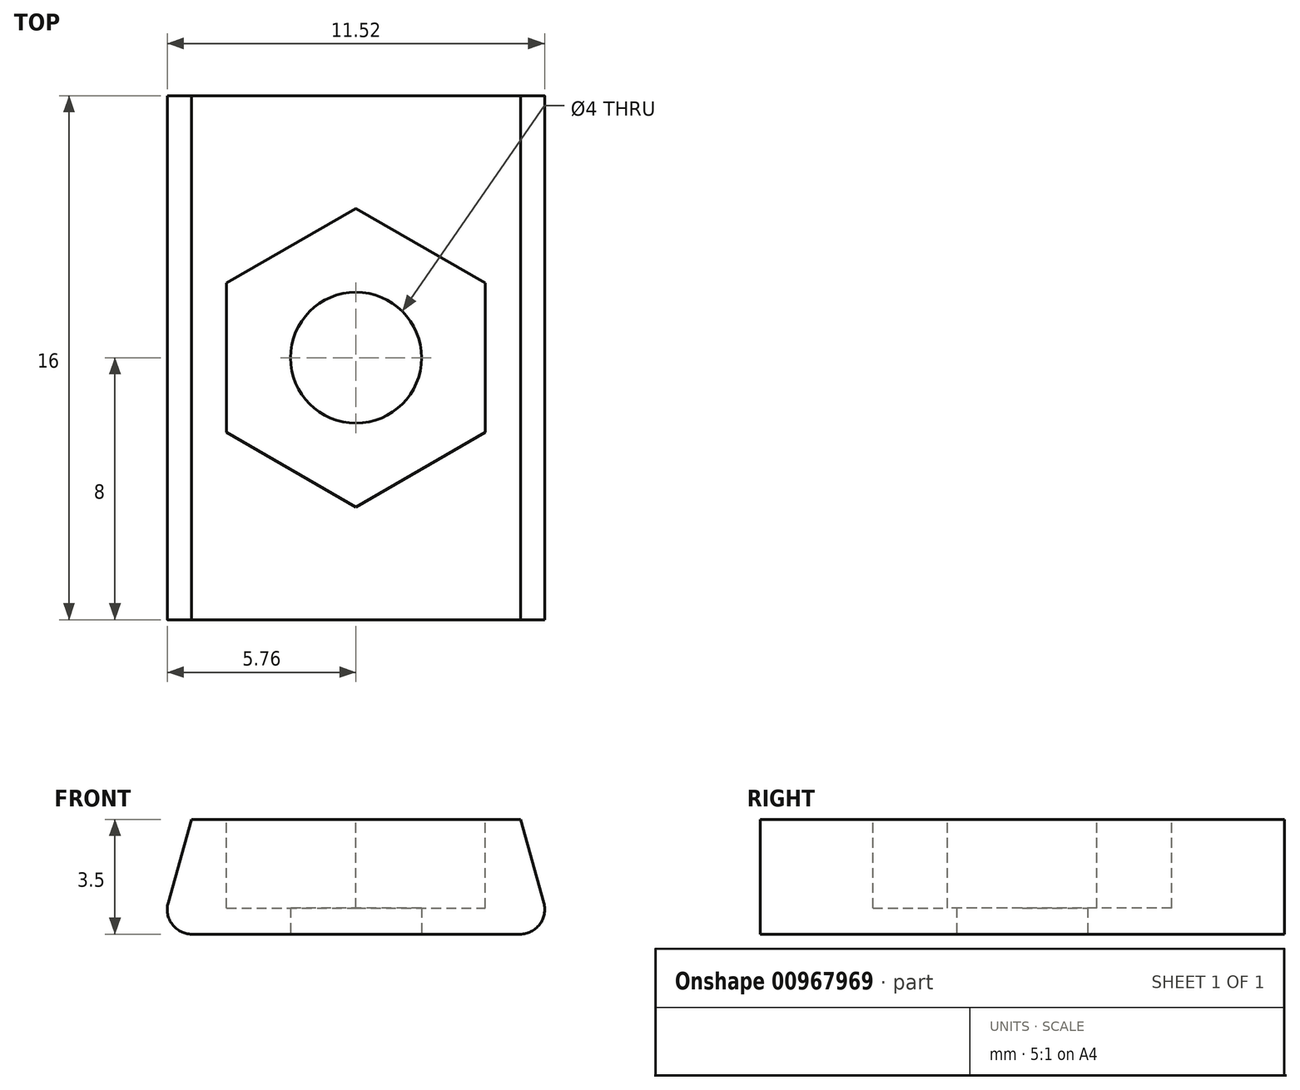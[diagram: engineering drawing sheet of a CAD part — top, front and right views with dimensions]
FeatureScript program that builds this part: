
annotation { "Feature Type Name" : "Feature", "Feature Type Description" : "" }
export const myFeature = defineFeature(function(context is Context, id is Id, definition is map)
    precondition{}
    {
        {
            var Q0;
            Q0=qCreatedBy(makeId("Front.planeOp"),FACE);
            var sketch = newSketch(context, id + "F0", { "sketchPlane" : qUnion([Q0])});
            skLineSegment(sketch, "E0.bottom", {"start": v(6, -2.5) * mm, "end": v(-6, -2.5) * mm});
            skLineSegment(sketch, "E0.top", {"start": v(6, 2.5) * mm, "end": v(-6, 2.5) * mm});
            skLineSegment(sketch, "E0.left", {"start": v(6, -2.5) * mm, "end": v(6, 2.5) * mm});
            skLineSegment(sketch, "E0.right", {"start": v(-6, -2.5) * mm, "end": v(-6, 2.5) * mm});
            skPoint(sketch, "E0.middle", {"position": v(0, 0) * mm});
            skLineSegment(sketch, "E1.bottom", {"start": v(4.6, -2.5) * mm, "end": v(-4.6, -2.5) * mm});
            skLineSegment(sketch, "E1.top", {"start": v(4.6, 2.5) * mm, "end": v(-4.6, 2.5) * mm});
            skLineSegment(sketch, "E1.left", {"start": v(4.6, -2.5) * mm, "end": v(4.6, 2.5) * mm});
            skLineSegment(sketch, "E1.right", {"start": v(-4.6, -2.5) * mm, "end": v(-4.6, 2.5) * mm});
            skLineSegment(sketch, "E2", {"start": v(-6, -2.5) * mm, "end": v(-4.6, 2.5) * mm});
            skLineSegment(sketch, "E3", {"start": v(4.6, 2.5) * mm, "end": v(6, -2.5) * mm});
            skPoint(sketch, "E4.middle", {"position": v(0, 2.5) * mm});
            skSolve(sketch);
        }
        {
            var Q0;
            {var subQ2=sQuery(id+"F0.wireOp",EDGE,"E1.right");Q0=makeQuery(id+"F0.imprint","IMPRINT",FACE,{"disambiguationData":[TD([[makeQuery(id+"F0.imprint","IMPRINT",EDGE,{"derivedFrom":subQ2}),1.0]])]});}
            var Q1;
            {var subQ0=sQuery(id+"F0.wireOp",EDGE,"E1.left");Q1=makeQuery(id+"F0.imprint","IMPRINT",FACE,{"disambiguationData":[TD([[makeQuery(id+"F0.imprint","IMPRINT",EDGE,{"derivedFrom":subQ0}),1.0]])]});}
            var Q2;
            {var subQ0=sQuery(id+"F0.wireOp",EDGE,"E1.left");Q2=makeQuery(id+"F0.imprint","IMPRINT",FACE,{"disambiguationData":[TD([[makeQuery(id+"F0.imprint","IMPRINT",EDGE,{"derivedFrom":subQ0}),-1.0]])]});}
            extrude(context, id + "F1", {"entities" : qUnion([Q0, Q1, Q2]), "endBound" : BoundingType.SYMMETRIC, "depth" : 16 * mm, "offsetDistance" : 25 * mm});
        }
        {
            var Q0;
            Q0=makeQuery(id+"F1.opExtrude","SWEPT_FACE",FACE,{"disambiguationData":[OSD([sQuery(id+"F0.wireOp",EDGE,"E0.bottom")])]});
            var sketch = newSketch(context, id + "F2", { "sketchPlane" : qUnion([Q0])});
            skLineSegment(sketch, "E5", {"start": v(0, 0) * mm, "end": v(0, 6) * mm});
            skLineSegment(sketch, "E6", {"start": v(0, 0) * mm, "end": v(0, -6) * mm});
            skCircle(sketch, "E7", {"center": v(0, -6) * mm, "radius": 1.5 * mm});
            skCircle(sketch, "E8", {"center": v(0, 6) * mm, "radius": 1.5 * mm});
            skCircle(sketch, "E9", {"center": v(0, 0) * mm, "radius": 2 * mm});
            skSolve(sketch);
        }
        {
            var Q0;
            {var subQ0=sQuery(id+"F0.wireOp",EDGE,"E0.top");Q0=qUnion([makeQuery(id+"F1.opExtrude","SWEPT_EDGE",EDGE,{"disambiguationData":[OSD([subQ0,sQuery(id+"F0.wireOp",EDGE,"E1.right"),sQuery(id+"F0.wireOp",EDGE,"E2")])]}),makeQuery(id+"F1.opExtrude","SWEPT_EDGE",EDGE,{"disambiguationData":[OSD([subQ0,sQuery(id+"F0.wireOp",EDGE,"E1.left"),sQuery(id+"F0.wireOp",EDGE,"E3")])]})]);}
            var Q1;
            Q1=makeQuery(id+"F1.opExtrude","SWEPT_EDGE",EDGE,{"disambiguationData":[OSD([sQuery(id+"F0.wireOp",EDGE,"E0.top"),sQuery(id+"F0.wireOp",EDGE,"E1.right"),sQuery(id+"F0.wireOp",EDGE,"E2")])]});
            var Q2;
            {var subQ0=sQuery(id+"F0.wireOp",EDGE,"E0.top");Q2=qUnion([makeQuery(id+"F1.opExtrude","SWEPT_EDGE",EDGE,{"disambiguationData":[OSD([subQ0,sQuery(id+"F0.wireOp",EDGE,"E1.right"),sQuery(id+"F0.wireOp",EDGE,"E2")])]}),makeQuery(id+"F1.opExtrude","SWEPT_EDGE",EDGE,{"disambiguationData":[OSD([subQ0,sQuery(id+"F0.wireOp",EDGE,"E1.left"),sQuery(id+"F0.wireOp",EDGE,"E3")])]})]);}
            var Q3;
            Q3=makeQuery(id+"F1.opExtrude","SWEPT_EDGE",EDGE,{"disambiguationData":[OSD([sQuery(id+"F0.wireOp",EDGE,"E0.top"),sQuery(id+"F0.wireOp",EDGE,"E1.left"),sQuery(id+"F0.wireOp",EDGE,"E3")])]});
            var Q4;
            Q4=makeQuery(id+"F1.opExtrude","SWEPT_EDGE",EDGE,{"disambiguationData":[OSD([sQuery(id+"F0.wireOp",EDGE,"E0.bottom"),sQuery(id+"F0.wireOp",EDGE,"E0.left"),sQuery(id+"F0.wireOp",EDGE,"E3")])]});
            var Q5;
            Q5=makeQuery(id+"F1.opExtrude","SWEPT_EDGE",EDGE,{"disambiguationData":[OSD([sQuery(id+"F0.wireOp",EDGE,"E0.bottom"),sQuery(id+"F0.wireOp",EDGE,"E0.right"),sQuery(id+"F0.wireOp",EDGE,"E2")])]});
            fillet(context, id + "F3", {"entities" : qUnion([Q0, Q1, Q2, Q3, Q4, Q5]), "radius" : .75 * mm, "tangentPropagation" : true, "allowEdgeOverflow" : false});
        }
        {
            var Q0;
            Q0=makeQuery(id+"F1.opExtrude","SWEPT_FACE",FACE,{"disambiguationData":[OSD([sQuery(id+"F0.wireOp",EDGE,"E0.top")])]});
            var sketch = newSketch(context, id + "F4", { "sketchPlane" : qUnion([Q0])});
            skPoint(sketch, "E10.0.midPoint", {"position": v(0, -4.82) * mm});
            skCircle(sketch, "E11.cCircle", {"center": v(0, 0) * mm, "radius": 3.95 * mm, "construction": true});
            skLineSegment(sketch, "E11.0", {"start": v(3.95, 2.28) * mm, "end": v(3.95, -2.28) * mm});
            skLineSegment(sketch, "E11.1", {"start": v(3.95, -2.28) * mm, "end": v(0, -4.56) * mm});
            skLineSegment(sketch, "E11.2", {"start": v(0, -4.56) * mm, "end": v(-3.95, -2.28) * mm});
            skLineSegment(sketch, "E11.3", {"start": v(-3.95, -2.28) * mm, "end": v(-3.95, 2.28) * mm});
            skLineSegment(sketch, "E11.4", {"start": v(-3.95, 2.28) * mm, "end": v(0, 4.56) * mm});
            skLineSegment(sketch, "E11.5", {"start": v(0, 4.56) * mm, "end": v(3.95, 2.28) * mm});
            skPoint(sketch, "E11.0.midPoint", {"position": v(3.95, 0) * mm});
            skSolve(sketch);
        }
        {
            var Q0;
            Q0=makeQuery(id+"F1.opExtrude","CAP_FACE",FACE,{"disambiguationData":[OSD([sQuery(id+"F0.wireOp",EDGE,"E0.bottom"),sQuery(id+"F0.wireOp",EDGE,"E0.top"),sQuery(id+"F0.wireOp",EDGE,"E2"),sQuery(id+"F0.wireOp",EDGE,"E3")])],"isStart":false});
            var sketch = newSketch(context, id + "F5", { "sketchPlane" : qUnion([Q0])});
            skLineSegment(sketch, "E12.bottom", {"start": v(7.37, 4) * mm, "end": v(-7.37, 4) * mm});
            skLineSegment(sketch, "E12.top", {"start": v(7.37, 1) * mm, "end": v(-7.37, 1) * mm});
            skLineSegment(sketch, "E12.left", {"start": v(7.37, 4) * mm, "end": v(7.37, 1) * mm});
            skLineSegment(sketch, "E12.right", {"start": v(-7.37, 4) * mm, "end": v(-7.37, 1) * mm});
            skPoint(sketch, "E12.middle", {"position": v(0, 2.5) * mm});
            skSolve(sketch);
        }
        {
            var Q0;
            Q0=makeQuery(id+"F5.imprint","IMPRINT",FACE,{"disambiguationData":[TD([[makeQuery(id+"F5.imprint","IMPRINT",EDGE,{"derivedFrom":sQuery(id+"F5.wireOp",EDGE,"E12.bottom")}),1.0]])]});
            var Q1;
            {var subQ0=sQuery(id+"F0.wireOp",EDGE,"E0.top");Q1=makeQuery(id+"F5.imprint","IMPRINT",FACE,{"disambiguationData":[TD([[makeQuery(id+"F5.imprint","IMPRINT",EDGE,{"derivedFrom":makeQuery(id+"F1.opExtrude","CAP_EDGE",EDGE,{"disambiguationData":[OSD([subQ0])],"isStart":false})}),1.0]])]});}
            extrude(context, id + "F6", {"entities" : qUnion([Q0, Q1]), "operationType" : NewBodyOperationType.REMOVE, "oppositeDirection" : true, "depth" : 30 * mm, "offsetDistance" : 25 * mm});
        }
        {
            var Q0;
            Q0=makeQuery(id+"F4.imprint","IMPRINT",FACE,{"disambiguationData":[TD([[makeQuery(id+"F4.imprint","IMPRINT",EDGE,{"derivedFrom":sQuery(id+"F4.wireOp",EDGE,"E11.0")}),-1.0]])]});
            extrude(context, id + "F7", {"entities" : qUnion([Q0]), "operationType" : NewBodyOperationType.REMOVE, "oppositeDirection" : true, "depth" : 4.2 * mm, "offsetDistance" : 25 * mm});
        }
        {
            var Q0;
            {var subQ0=sQuery(id+"F2.wireOp",EDGE,"E6");var subQ1=sQuery(id+"F2.wireOp",EDGE,"E5");var subQ2=makeQuery(id+"F2.imprint","INTERSECT",VERTEX,{"derivedFrom":[subQ1,subQ0]});Q0=makeQuery(id+"F2.imprint","IMPRINT",FACE,{"disambiguationData":[TD([[makeQuery(id+"F2.imprint","IMPRINT",EDGE,{"disambiguationData":[TD([[subQ2,-1.0]])],"derivedFrom":subQ1}),1.0]])]});}
            var Q1;
            {var subQ0=sQuery(id+"F2.wireOp",EDGE,"E6");var subQ1=sQuery(id+"F2.wireOp",EDGE,"E5");var subQ2=makeQuery(id+"F2.imprint","INTERSECT",VERTEX,{"derivedFrom":[subQ1,subQ0]});Q1=makeQuery(id+"F2.imprint","IMPRINT",FACE,{"disambiguationData":[TD([[makeQuery(id+"F2.imprint","IMPRINT",EDGE,{"disambiguationData":[TD([[subQ2,-1.0]])],"derivedFrom":subQ1}),-1.0]])]});}
            extrude(context, id + "F8", {"entities" : qUnion([Q0, Q1]), "operationType" : NewBodyOperationType.REMOVE, "oppositeDirection" : true, "depth" : 25 * mm, "offsetDistance" : 25 * mm});
        }
    });
